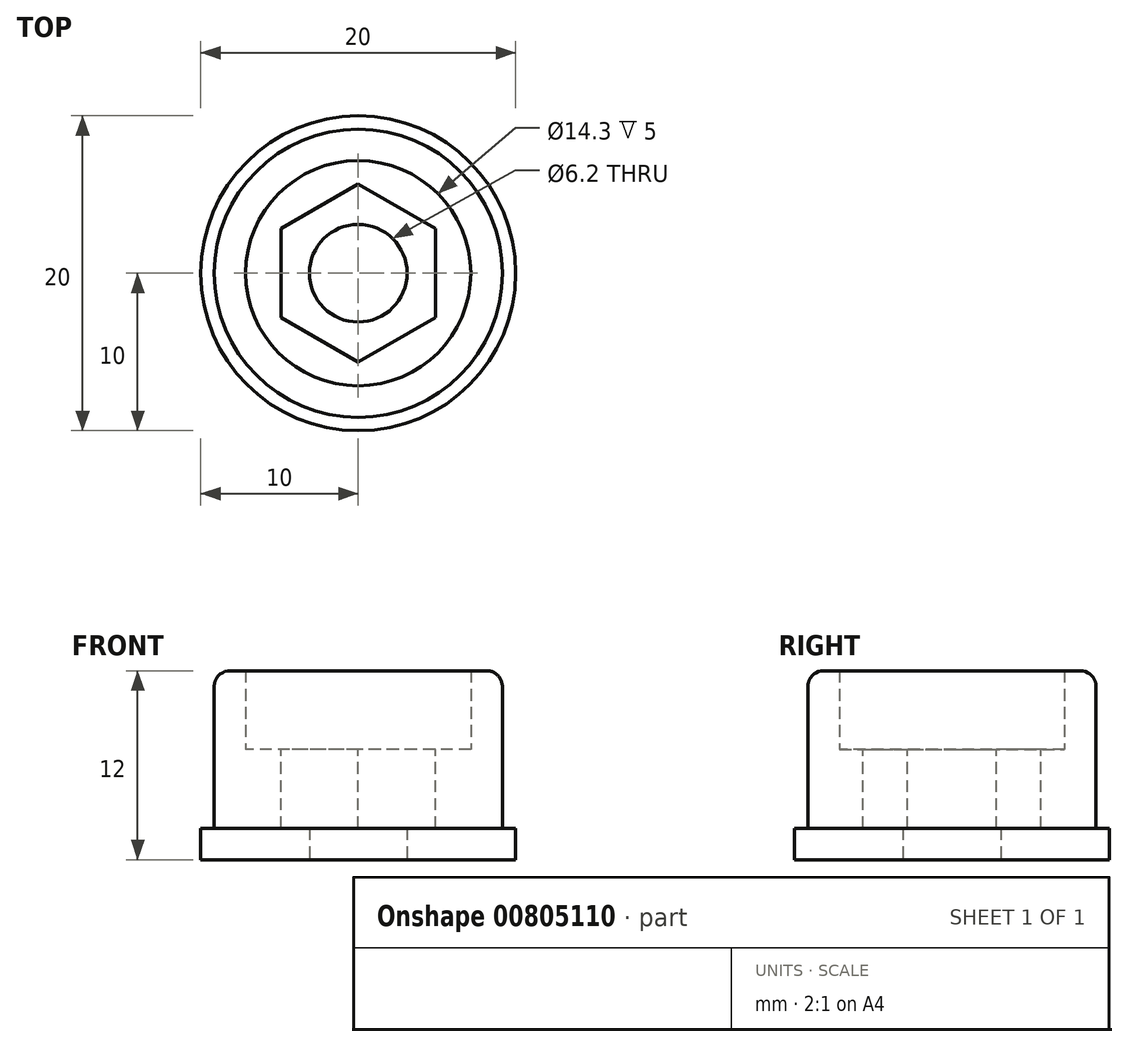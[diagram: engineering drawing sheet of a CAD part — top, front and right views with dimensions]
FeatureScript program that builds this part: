
annotation { "Feature Type Name" : "Feature", "Feature Type Description" : "" }
export const myFeature = defineFeature(function(context is Context, id is Id, definition is map)
    precondition{}
    {
        {
            var Q0;
            Q0=qCreatedBy(makeId("Top.planeOp"),FACE);
            var sketch = newSketch(context, id + "F0", { "sketchPlane" : qUnion([Q0])});
            skCircle(sketch, "E0", {"center": v(0, 0) * mm, "radius": 10 * mm});
            skSolve(sketch);
        }
        {
            var Q0;
            Q0 = qSketchRegion(id + "F0", true);
            extrude(context, id + "F1", {"entities" : qUnion([Q0]), "oppositeDirection" : true, "depth" : 2 * mm, "offsetDistance" : 25 * mm});
        }
        {
            var Q0;
            Q0=makeQuery(id+"F1.opExtrude","CAP_FACE",FACE,{"disambiguationData":[OSD([sQuery(id+"F0.wireOp",EDGE,"E0")])],"isStart":true});
            var sketch = newSketch(context, id + "F2", { "sketchPlane" : qUnion([Q0])});
            skCircle(sketch, "E1", {"center": v(0, 0) * mm, "radius": 9.15 * mm});
            skSolve(sketch);
        }
        {
            var Q0;
            Q0 = qSketchRegion(id + "F2", true);
            extrude(context, id + "F3", {"entities" : qUnion([Q0]), "operationType" : NewBodyOperationType.ADD, "depth" : 5 * mm, "offsetDistance" : 25 * mm});
        }
        {
            var Q0;
            Q0=makeQuery(id+"F3.opExtrude","CAP_FACE",FACE,{"disambiguationData":[OSD([sQuery(id+"F2.wireOp",EDGE,"E1")])],"isStart":false});
            var sketch = newSketch(context, id + "F4", { "sketchPlane" : qUnion([Q0])});
            skCircle(sketch, "E2.cCircle", {"center": v(0, 0) * mm, "radius": 5.65 * mm, "construction": true});
            skLineSegment(sketch, "E2.0", {"start": v(0, 5.65) * mm, "end": v(4.9, 2.82) * mm});
            skLineSegment(sketch, "E2.1", {"start": v(4.9, 2.82) * mm, "end": v(4.9, -2.82) * mm});
            skLineSegment(sketch, "E2.2", {"start": v(4.9, -2.82) * mm, "end": v(0, -5.65) * mm});
            skLineSegment(sketch, "E2.3", {"start": v(0, -5.65) * mm, "end": v(-4.9, -2.83) * mm});
            skLineSegment(sketch, "E2.4", {"start": v(-4.9, -2.83) * mm, "end": v(-4.9, 2.82) * mm});
            skLineSegment(sketch, "E2.5", {"start": v(-4.9, 2.82) * mm, "end": v(0, 5.65) * mm});
            skSolve(sketch);
        }
        {
            var Q0;
            Q0 = qSketchRegion(id + "F4", true);
            extrude(context, id + "F5", {"entities" : qUnion([Q0]), "operationType" : NewBodyOperationType.REMOVE, "oppositeDirection" : true, "depth" : 5 * mm, "offsetDistance" : 25 * mm});
        }
        {
            var Q0;
            Q0=makeQuery(id+"F3.opExtrude","CAP_FACE",FACE,{"disambiguationData":[OSD([sQuery(id+"F2.wireOp",EDGE,"E1")])],"isStart":false});
            var sketch = newSketch(context, id + "F6", { "sketchPlane" : qUnion([Q0])});
            skCircle(sketch, "E3", {"center": v(0, 0) * mm, "radius": 9.15 * mm});
            skCircle(sketch, "E4", {"center": v(0, 0) * mm, "radius": 7.15 * mm});
            skSolve(sketch);
        }
        {
            var Q0;
            Q0 = qSketchRegion(id + "F6", true);
            extrude(context, id + "F7", {"entities" : qUnion([Q0]), "operationType" : NewBodyOperationType.ADD, "depth" : 5 * mm, "offsetDistance" : 25 * mm});
        }
        {
            var Q0;
            Q0=makeQuery(id+"F1.opExtrude","CAP_FACE",FACE,{"disambiguationData":[OSD([sQuery(id+"F0.wireOp",EDGE,"E0")])],"isStart":false});
            var sketch = newSketch(context, id + "F8", { "sketchPlane" : qUnion([Q0])});
            skCircle(sketch, "E5", {"center": v(0, 0) * mm, "radius": 3.1 * mm});
            skSolve(sketch);
        }
        {
            var Q0;
            Q0 = qSketchRegion(id + "F8", true);
            extrude(context, id + "F9", {"entities" : qUnion([Q0]), "operationType" : NewBodyOperationType.REMOVE, "endBound" : BoundingType.THROUGH_ALL, "oppositeDirection" : true, "depth" : 25 * mm, "offsetDistance" : 25 * mm});
        }
        {
            var Q0;
            Q0=makeQuery(id+"F7.opExtrude","CAP_EDGE",EDGE,{"disambiguationData":[OSD([sQuery(id+"F6.wireOp",EDGE,"E3")])],"isStart":false});
            fillet(context, id + "F10", {"entities" : qUnion([Q0]), "radius" : 1 * mm, "tangentPropagation" : true, "allowEdgeOverflow" : false});
        }
    });
